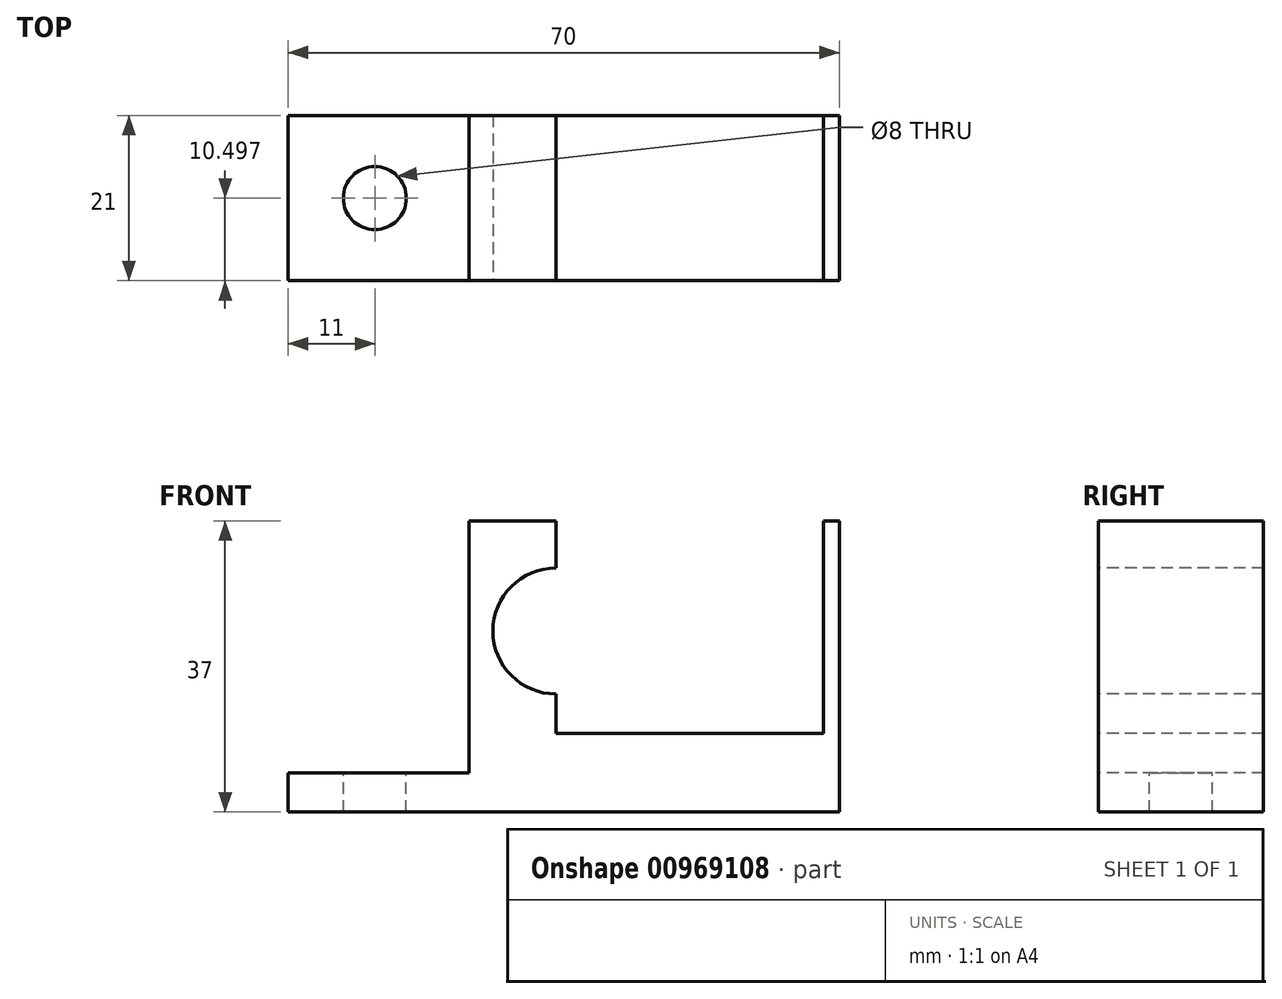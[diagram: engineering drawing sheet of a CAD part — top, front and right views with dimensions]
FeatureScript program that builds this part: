
annotation { "Feature Type Name" : "Feature", "Feature Type Description" : "" }
export const myFeature = defineFeature(function(context is Context, id is Id, definition is map)
    precondition{}
    {
        {
            var Q0;
            Q0=qCreatedBy(makeId("Top.planeOp"),FACE);
            var sketch = newSketch(context, id + "F0", { "sketchPlane" : qUnion([Q0])});
            skLineSegment(sketch, "E0.bottom", {"start": v(-85.12, 12.63) * mm, "end": v(-15.12, 12.63) * mm});
            skLineSegment(sketch, "E0.top", {"start": v(-85.12, -8.37) * mm, "end": v(-15.12, -8.37) * mm});
            skLineSegment(sketch, "E0.left", {"start": v(-85.12, 12.63) * mm, "end": v(-85.12, -8.37) * mm});
            skLineSegment(sketch, "E0.right", {"start": v(-15.12, 12.63) * mm, "end": v(-15.12, -8.37) * mm});
            skSolve(sketch);
        }
        {
            var Q0;
            Q0=makeQuery(id+"F0.imprint","IMPRINT",FACE,{"disambiguationData":[TD([[makeQuery(id+"F0.imprint","IMPRINT",EDGE,{"derivedFrom":sQuery(id+"F0.wireOp",EDGE,"E0.bottom")}),-1.0]])]});
            extrude(context, id + "F1", {"entities" : qUnion([Q0]), "depth" : 37 * mm, "offsetDistance" : 25 * mm});
        }
        {
            var Q0;
            Q0=makeQuery(id+"F1.opExtrude","CAP_FACE",FACE,{"disambiguationData":[OSD([sQuery(id+"F0.wireOp",EDGE,"E0.bottom"),sQuery(id+"F0.wireOp",EDGE,"E0.top"),sQuery(id+"F0.wireOp",EDGE,"E0.left"),sQuery(id+"F0.wireOp",EDGE,"E0.right")])],"isStart":false});
            var sketch = newSketch(context, id + "F2", { "sketchPlane" : qUnion([Q0])});
            skLineSegment(sketch, "E1.bottom", {"start": v(-17.12, 12.63) * mm, "end": v(-51.12, 12.63) * mm});
            skLineSegment(sketch, "E1.top", {"start": v(-17.12, -8.37) * mm, "end": v(-51.12, -8.37) * mm});
            skLineSegment(sketch, "E1.left", {"start": v(-17.12, 12.63) * mm, "end": v(-17.12, -8.37) * mm});
            skLineSegment(sketch, "E1.right", {"start": v(-51.12, 12.63) * mm, "end": v(-51.12, -8.37) * mm});
            skSolve(sketch);
        }
        {
            var Q0;
            Q0=makeQuery(id+"F2.imprint","IMPRINT",FACE,{"disambiguationData":[TD([[makeQuery(id+"F2.imprint","IMPRINT",EDGE,{"derivedFrom":sQuery(id+"F2.wireOp",EDGE,"E1.bottom")}),-1.0]])]});
            extrude(context, id + "F3", {"entities" : qUnion([Q0]), "operationType" : NewBodyOperationType.REMOVE, "oppositeDirection" : true, "depth" : 27 * mm, "offsetDistance" : 25 * mm});
        }
        {
            var Q0;
            Q0=makeQuery(id+"F1.opExtrude","SWEPT_FACE",FACE,{"disambiguationData":[OSD([sQuery(id+"F0.wireOp",EDGE,"E0.top")])]});
            var sketch = newSketch(context, id + "F4", { "sketchPlane" : qUnion([Q0])});
            skArc(sketch, "E2", {"start": v(-51.12, 31) * mm, "mid": v(-59.12, 23) * mm, "end": v(-51.12, 15) * mm});
            skSolve(sketch);
        }
        {
            var Q0;
            {var subQ0=sQuery(id+"F4.wireOp",EDGE,"E2");Q0=makeQuery(id+"F4.imprint","IMPRINT",FACE,{"disambiguationData":[TD([[makeQuery(id+"F4.imprint","IMPRINT",EDGE,{"derivedFrom":subQ0}),1.0]])]});}
            extrude(context, id + "F5", {"entities" : qUnion([Q0]), "operationType" : NewBodyOperationType.REMOVE, "oppositeDirection" : true, "depth" : 21 * mm, "offsetDistance" : 25 * mm});
        }
        {
            var Q0;
            {var subQ0=sQuery(id+"F0.wireOp",EDGE,"E0.bottom");var subQ1=sQuery(id+"F0.wireOp",EDGE,"E0.top");var subQ2=sQuery(id+"F0.wireOp",EDGE,"E0.left");Q0=makeQuery(id+"F3.boolean.opBoolean","SPLIT",FACE,{"disambiguationData":[TD([makeQuery(id+"F1.opExtrude","SWEPT_FACE",FACE,{"disambiguationData":[OSD([subQ2])]})])],"derivedFrom":makeQuery(id+"F1.opExtrude","CAP_FACE",FACE,{"disambiguationData":[OSD([subQ0,subQ1,subQ2,sQuery(id+"F0.wireOp",EDGE,"E0.right")])],"isStart":false})});}
            var sketch = newSketch(context, id + "F6", { "sketchPlane" : qUnion([Q0])});
            skLineSegment(sketch, "E3.bottom", {"start": v(-85.12, 12.63) * mm, "end": v(-62.12, 12.63) * mm});
            skLineSegment(sketch, "E3.top", {"start": v(-85.12, -8.37) * mm, "end": v(-62.12, -8.37) * mm});
            skLineSegment(sketch, "E3.left", {"start": v(-85.12, 12.63) * mm, "end": v(-85.12, -8.37) * mm});
            skLineSegment(sketch, "E3.right", {"start": v(-62.12, 12.63) * mm, "end": v(-62.12, -8.37) * mm});
            skSolve(sketch);
        }
        {
            var Q0;
            Q0=makeQuery(id+"F6.imprint","IMPRINT",FACE,{"disambiguationData":[TD([[makeQuery(id+"F6.imprint","IMPRINT",EDGE,{"derivedFrom":sQuery(id+"F6.wireOp",EDGE,"E3.bottom")}),-1.0]])]});
            extrude(context, id + "F7", {"entities" : qUnion([Q0]), "operationType" : NewBodyOperationType.REMOVE, "oppositeDirection" : true, "depth" : 32 * mm, "offsetDistance" : 25 * mm});
        }
        {
            var Q0;
            Q0=makeQuery(id+"F7.boolean.opBoolean","COPY",FACE,{"derivedFrom":makeQuery(id+"F7.opExtrude","CAP_FACE",FACE,{"disambiguationData":[OSD([sQuery(id+"F6.wireOp",EDGE,"E3.bottom"),sQuery(id+"F6.wireOp",EDGE,"E3.top"),sQuery(id+"F6.wireOp",EDGE,"E3.left"),sQuery(id+"F6.wireOp",EDGE,"E3.right")])],"isStart":false})});
            var sketch = newSketch(context, id + "F8", { "sketchPlane" : qUnion([Q0])});
            skCircle(sketch, "E4", {"center": v(-74.12, 2.13) * mm, "radius": 3.75 * mm});
            skSolve(sketch);
        }
        {
            var Q0;
            Q0=sQuery(id+"F8.wireOp",VERTEX,"E4.center");
            var Q1;
            Q1=makeQuery(id+"F1.opExtrude","SWEPT_BODY",BODY,{"disambiguationData":[OSD([sQuery(id+"F0.wireOp",EDGE,"E0.bottom"),sQuery(id+"F0.wireOp",EDGE,"E0.top"),sQuery(id+"F0.wireOp",EDGE,"E0.left"),sQuery(id+"F0.wireOp",EDGE,"E0.right")])]});
            hole(context, id + "F9", {"style" : HoleStyle.SIMPLE, "endStyle" : HoleEndStyle.THROUGH, "holeDiameter" : 8 * mm, "majorDiameter" : 5 * mm, "isTappedThrough" : true, "tappedDepth" : 12 * mm, "tapClearance" : 3, "startFromSketch" : true, "locations" : qUnion([Q0]), "scope" : qUnion([Q1])});
        }
    });
